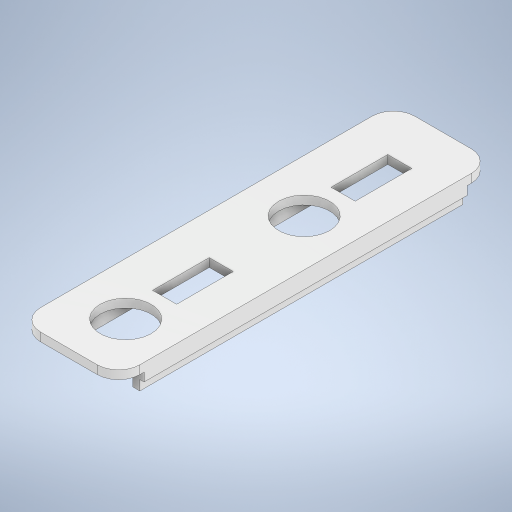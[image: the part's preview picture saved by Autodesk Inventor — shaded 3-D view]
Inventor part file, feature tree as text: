
AUTODESK INVENTOR PART (.ipt)
format: ipt  version: 2024.1 (Build 281209000, 209)  size: 326,144 bytes
history: native  units: mm
features: extrude x3, sketch x2, other x1
ambient origin geometry x8: Origin, YZ Plane, XZ Plane, XY Plane, X Axis, Y Axis, Z Axis, Center Point
bodies: Body1 (feature_tree)
feature tree (6):
  other  "Sólido1"
  extrude  "Extrusión1"  Depth=132.0mm
  sketch  "Boceto2"  dims[d2=7.5mm d5=8.5mm d8=20.0mm d9=12.0mm d10=43.0mm d11=16.5mm d12=13.5mm d13=16.5mm d15=18.0mm d16=13.5mm d17=3.0mm d18=0.0mm d19=4.0mm d20=114.0mm d21=2.5mm d22=2.5mm d23=24.0mm d24=6.5mm d25=0.0mm d26=3.0mm d27=0.0mm d28=0.5mm d29=0.872665mm]
  extrude  "Extrusión2"  Depth=8.5mm
  extrude  "Extrusión3"  Depth=20.0mm
  sketch  "Boceto1"  dims[d0=35.0mm d1=132.0mm]
